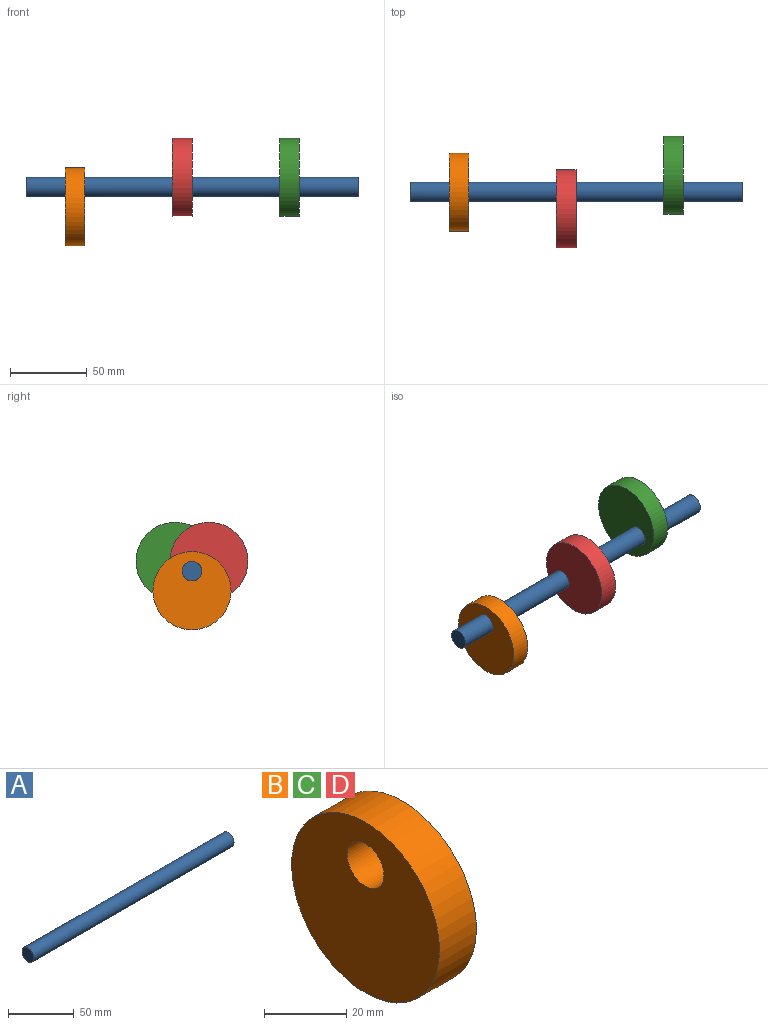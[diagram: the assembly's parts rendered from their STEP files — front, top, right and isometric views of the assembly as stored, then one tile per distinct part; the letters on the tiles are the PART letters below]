
ASSEMBLY  parts=4 mates=3
PART A: 3 faces, bbox 215.9x12.7x12.7 mm
  f0: plane 12.7x12.7mm, normal (-1,0,0), area 126.7mm2, adj f2
  f1: plane 12.7x12.7mm, normal (1,0,0), area 126.7mm2, adj f2
  f2: cylinder r=6.35mm len=215.9mm, axis (-1,0,0), area 8614mm2, adj f0,f1
PART B: 4 faces, bbox 12.7x50.8x50.8 mm
  f0: plane 50.8x50.8mm, normal (1,0,0), area 1900.2mm2, adj f2,f3
  f1: plane 50.8x50.8mm, normal (-1,0,0), area 1900.2mm2, adj f2,f3
  f2: cylinder r=25.4mm len=50.8mm, axis (-1,0,0), area 2026.8mm2, adj f0,f1
  f3: cylinder r=6.35mm len=12.7mm, axis (-1,0,0), area 506.7mm2, adj f0,f1
PART C: same geometry as B
PART D: same geometry as B
PLACE A rot(axis=(-1,0,0),90deg) t=(-114.3,-57.15,0)mm
PLACE B t=(-114.3,0,-57.15)mm
PLACE C rot(axis=(1,0,0),120deg) t=(25.4,49.49,28.58)mm
PLACE D rot(axis=(-1,0,0),120deg) t=(-44.45,-49.49,28.57)mm
MATE fastened D.f3 <-> A.f2  axis (-1,0,0) through (-114.3,0,0)mm
MATE fastened B.f3 <-> A.f2  axis (-1,0,0) through (-184.15,0,0)mm
MATE fastened C.f3 <-> A.f2  axis (-1,0,0) through (-44.45,0,0)mm
